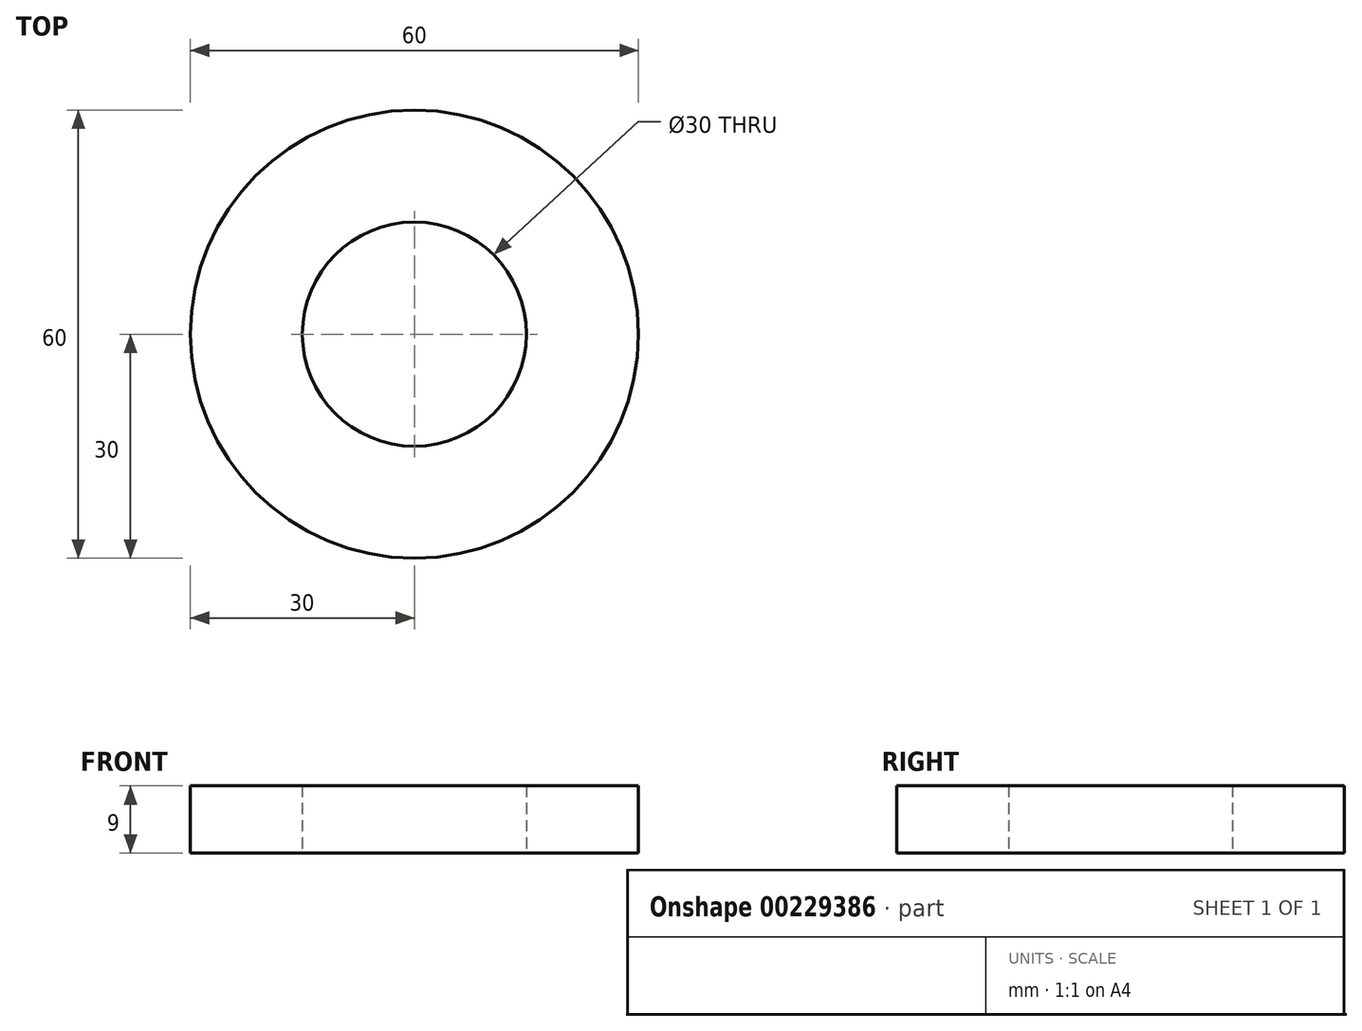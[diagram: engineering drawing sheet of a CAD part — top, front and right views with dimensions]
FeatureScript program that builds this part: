
annotation { "Feature Type Name" : "Feature", "Feature Type Description" : "" }
export const myFeature = defineFeature(function(context is Context, id is Id, definition is map)
    precondition{}
    {
        {
            var Q0;
            Q0=qCreatedBy(makeId("Top.planeOp"),FACE);
            var sketch = newSketch(context, id + "F0", { "sketchPlane" : qUnion([Q0])});
            skCircle(sketch, "E0", {"center": v(0, 0) * mm, "radius": 15 * mm});
            skCircle(sketch, "E1", {"center": v(0, 0) * mm, "radius": 30 * mm});
            skSolve(sketch);
        }
        {
            var Q0;
            Q0 = qSketchRegion(id + "F0", true);
            extrude(context, id + "F1", {"entities" : qUnion([Q0]), "depth" : 9 * mm});
        }
    });
